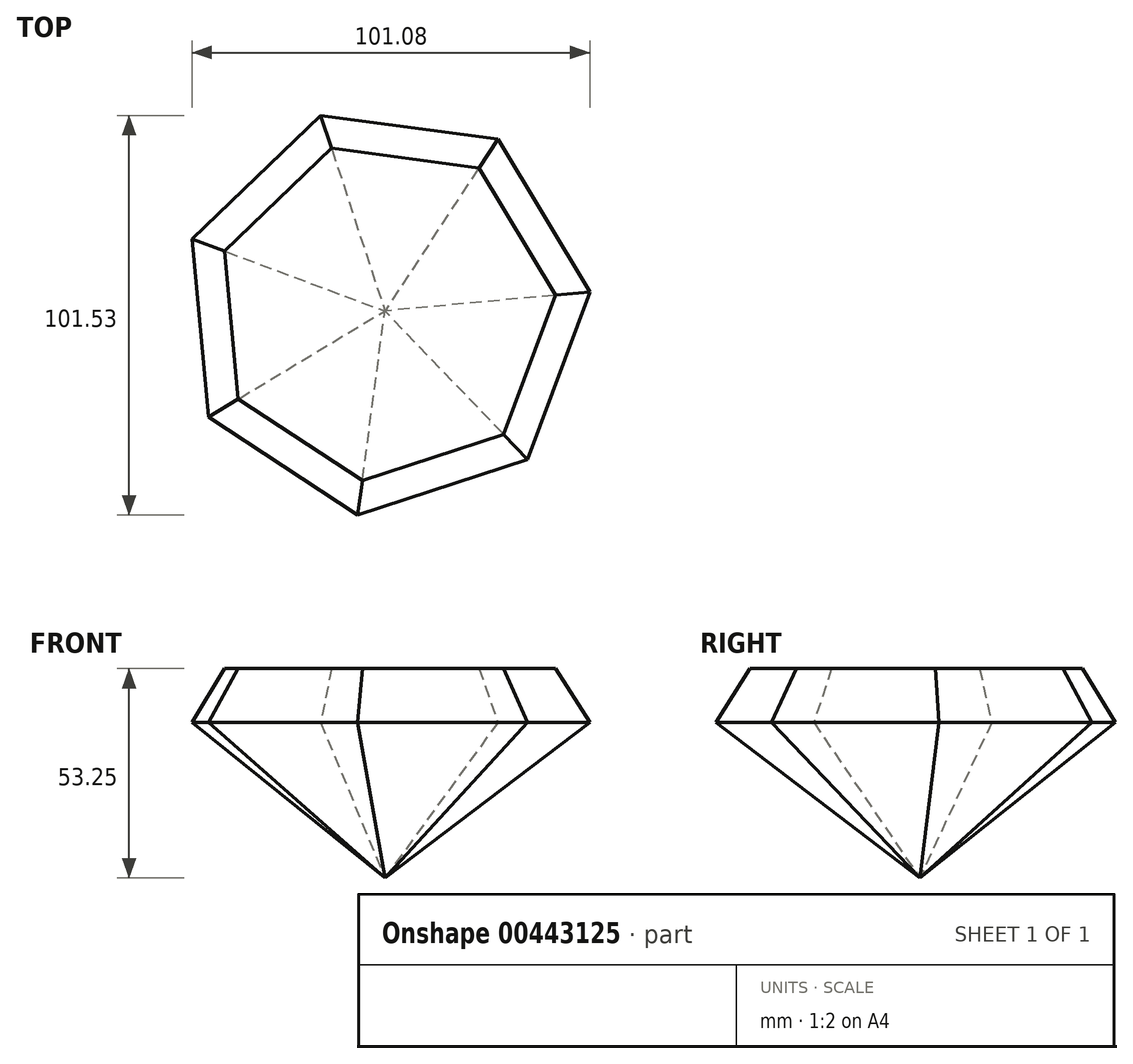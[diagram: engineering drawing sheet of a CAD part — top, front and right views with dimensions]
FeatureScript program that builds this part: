
annotation { "Feature Type Name" : "Feature", "Feature Type Description" : "" }
export const myFeature = defineFeature(function(context is Context, id is Id, definition is map)
    precondition{}
    {
        {
            var Q0;
            Q0=qCreatedBy(makeId("Top.planeOp"),FACE);
            var sketch = newSketch(context, id + "F0", { "sketchPlane" : qUnion([Q0])});
            skCircle(sketch, "E0.cCircle", {"center": v(0, 0) * mm, "radius": 47.12 * mm, "construction": true});
            skLineSegment(sketch, "E0.0", {"start": v(28.7, 43.72) * mm, "end": v(52.07, 4.82) * mm});
            skLineSegment(sketch, "E0.1", {"start": v(52.07, 4.82) * mm, "end": v(36.23, -37.7) * mm});
            skLineSegment(sketch, "E0.2", {"start": v(36.23, -37.7) * mm, "end": v(-6.89, -51.84) * mm});
            skLineSegment(sketch, "E0.3", {"start": v(-6.89, -51.84) * mm, "end": v(-44.82, -26.94) * mm});
            skLineSegment(sketch, "E0.4", {"start": v(-44.82, -26.94) * mm, "end": v(-49, 18.25) * mm});
            skLineSegment(sketch, "E0.5", {"start": v(-49, 18.25) * mm, "end": v(-16.29, 49.7) * mm});
            skLineSegment(sketch, "E0.6", {"start": v(-16.29, 49.7) * mm, "end": v(28.7, 43.72) * mm});
            skPoint(sketch, "E0.0.midPoint", {"position": v(40.38, 24.27) * mm});
            skSolve(sketch);
        }
        {
            var Q0;
            Q0 = qSketchRegion(id + "F0", true);
            extrude(context, id + "F1", {"entities" : qUnion([Q0]), "depth" : 13.72 * mm, "hasDraft" : true, "draftAngle" : 30 * degree, "draftPullDirection" : true, "hasSecondDirection" : true, "secondDirectionOppositeDirection" : true, "secondDirectionDepth" : 50.04 * mm, "hasSecondDirectionDraft" : true, "secondDirectionDraftAngle" : 50 * degree, "secondDirectionDraftPullDirection" : true});
        }
    });
